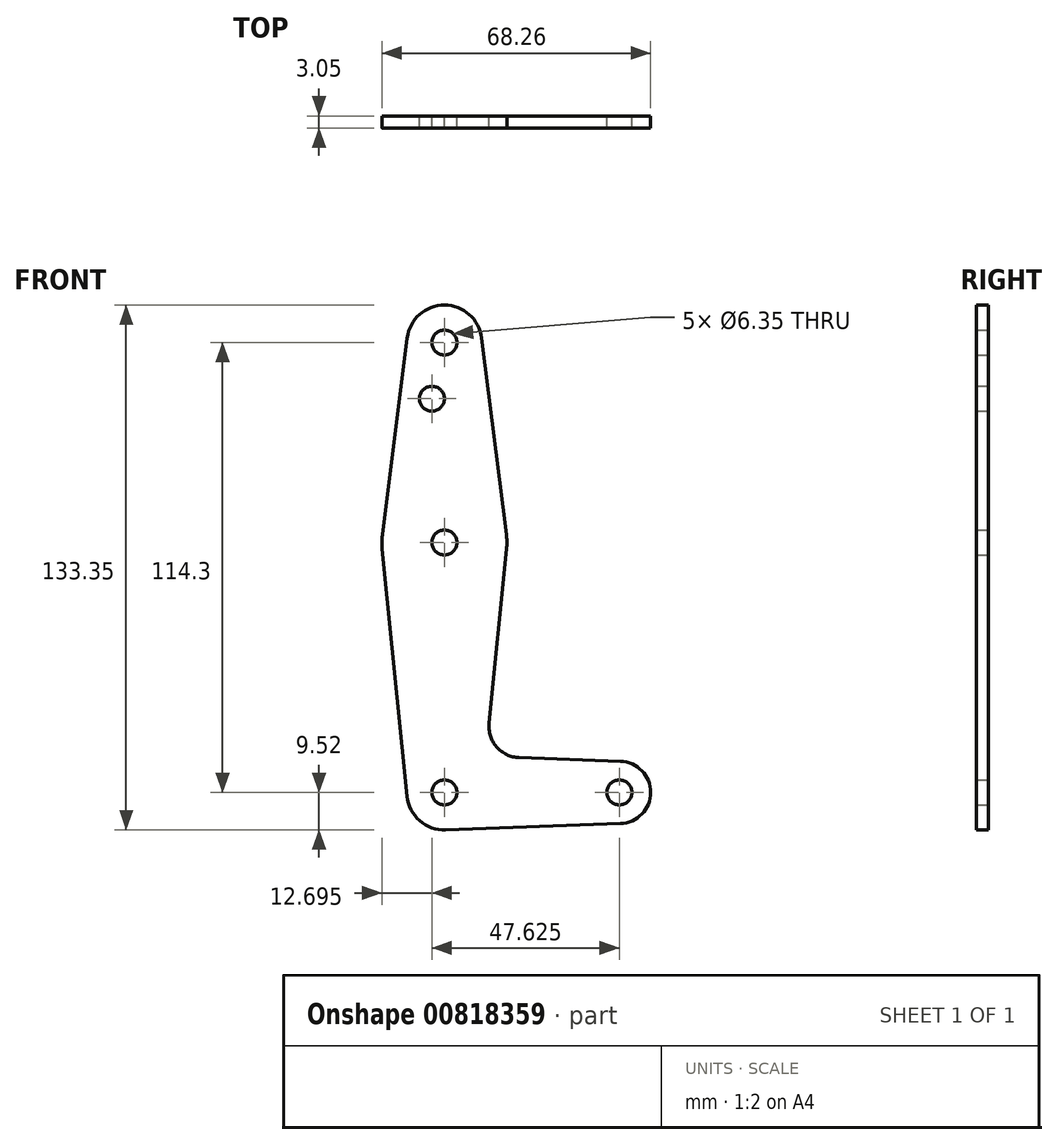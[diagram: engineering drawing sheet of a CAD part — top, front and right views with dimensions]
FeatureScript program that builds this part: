
annotation { "Feature Type Name" : "Feature", "Feature Type Description" : "" }
export const myFeature = defineFeature(function(context is Context, id is Id, definition is map)
    precondition{}
    {
        {
            var Q0;
            Q0=qCreatedBy(makeId("Front.planeOp"),FACE);
            var sketch = newSketch(context, id + "F0", { "sketchPlane" : qUnion([Q0])});
            skCircle(sketch, "E0", {"center": v(0, 0) * mm, "radius": 9.53 * mm});
            skCircle(sketch, "E1", {"center": v(0, 63.5) * mm, "radius": 15.88 * mm});
            skCircle(sketch, "E2", {"center": v(0, 114.3) * mm, "radius": 9.53 * mm});
            skCircle(sketch, "E3", {"center": v(44.45, 0) * mm, "radius": 7.94 * mm});
            skLineSegment(sketch, "E4", {"start": v(0, 114.3) * mm, "end": v(0, 0) * mm, "construction": true});
            skLineSegment(sketch, "E5", {"start": v(44.45, 0) * mm, "end": v(0, 0) * mm, "construction": true});
            skLineSegment(sketch, "E6", {"start": v(-9.45, 115.5) * mm, "end": v(-15.75, 65.48) * mm});
            skLineSegment(sketch, "E7", {"start": v(-15.8, 61.91) * mm, "end": v(-9.48, -0.95) * mm});
            skLineSegment(sketch, "E8", {"start": v(11.34, 17.6) * mm, "end": v(15.8, 61.91) * mm});
            skLineSegment(sketch, "E9", {"start": v(15.75, 65.48) * mm, "end": v(9.45, 115.5) * mm});
            skCircle(sketch, "E10", {"center": v(0, 114.3) * mm, "radius": 3.18 * mm});
            skCircle(sketch, "E11", {"center": v(-3.17, 100.03) * mm, "radius": 3.18 * mm});
            skCircle(sketch, "E12", {"center": v(0, 63.5) * mm, "radius": 3.18 * mm});
            skCircle(sketch, "E13", {"center": v(0, 0) * mm, "radius": 3.18 * mm});
            skCircle(sketch, "E14", {"center": v(44.45, 0) * mm, "radius": 3.18 * mm});
            skLineSegment(sketch, "E15", {"start": v(18.97, 8.85) * mm, "end": v(44.73, 7.93) * mm});
            skLineSegment(sketch, "E16", {"start": v(0.34, -9.52) * mm, "end": v(44.73, -7.93) * mm});
            skArc(sketch, "E17.filletArc", {"start": v(11.34, 17.6) * mm, "mid": v(13.26, 11.57) * mm, "end": v(18.97, 8.85) * mm});
            skSolve(sketch);
        }
        {
            var Q0;
            Q0=qSketchRegion(id+"F0",true);
            extrude(context, id + "F1", {"entities" : qUnion([Q0]), "depth" : 3.05 * mm, "offsetDistance" : 25.4 * mm});
        }
    });
